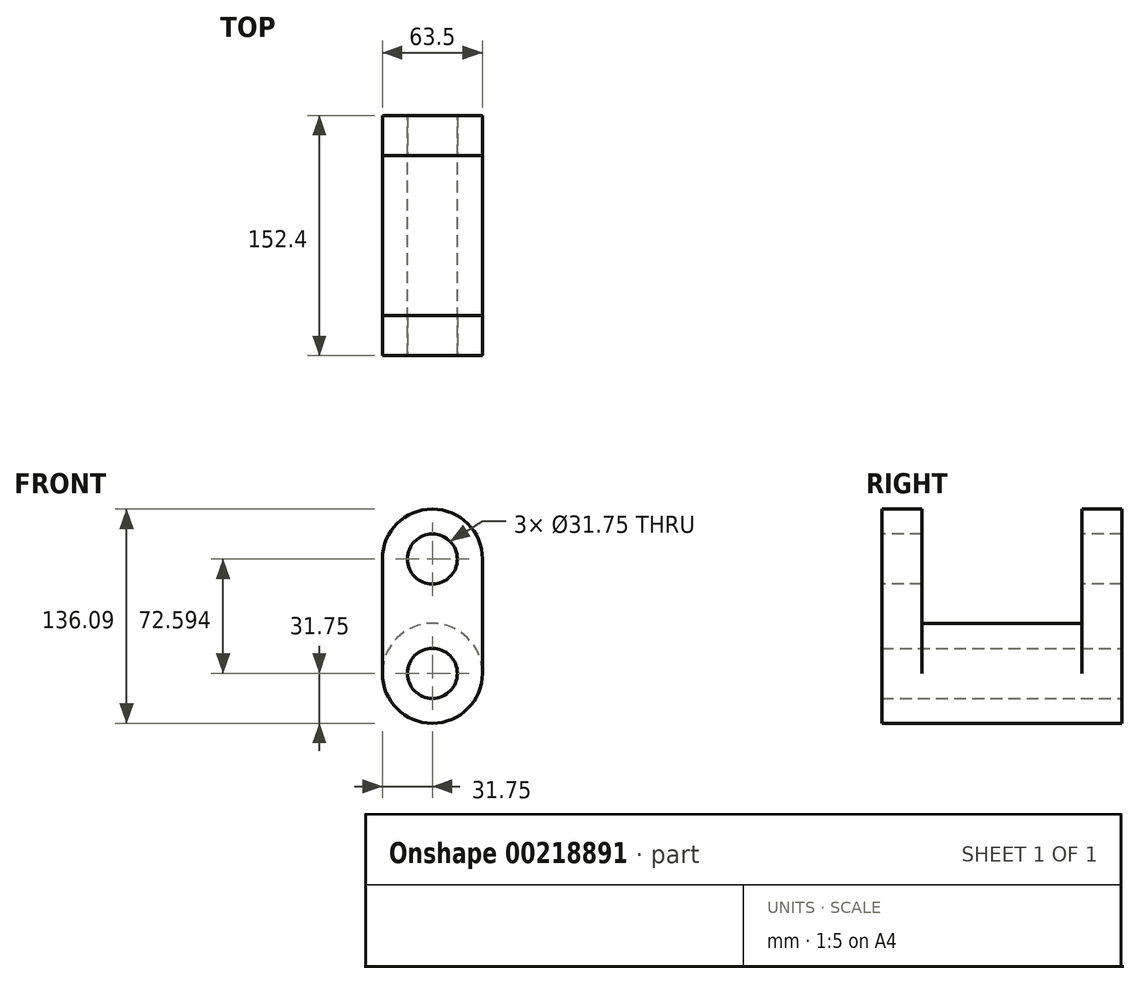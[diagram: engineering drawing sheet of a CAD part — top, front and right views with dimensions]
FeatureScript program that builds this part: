
annotation { "Feature Type Name" : "Feature", "Feature Type Description" : "" }
export const myFeature = defineFeature(function(context is Context, id is Id, definition is map)
    precondition{}
    {
        {
            var Q0;
            Q0=qCreatedBy(makeId("Front.planeOp"),FACE);
            var sketch = newSketch(context, id + "F0", { "sketchPlane" : qUnion([Q0])});
            skCircle(sketch, "E0", {"center": v(0, 0) * mm, "radius": 15.87 * mm});
            skCircle(sketch, "E1", {"center": v(0, 0) * mm, "radius": 31.75 * mm});
            skSolve(sketch);
        }
        {
            var Q0;
            Q0 = qSketchRegion(id + "F0", true);
            extrude(context, id + "F1", {"entities" : qUnion([Q0]), "endBound" : BoundingType.SYMMETRIC, "depth" : 152.4 * mm});
        }
        {
            var Q0;
            Q0=makeQuery(id+"F1.opExtrude","CAP_FACE",FACE,{"disambiguationData":[OSD([sQuery(id+"F0.wireOp",EDGE,"E0"),sQuery(id+"F0.wireOp",EDGE,"E1")])],"isStart":false});
            var sketch = newSketch(context, id + "F2", { "sketchPlane" : qUnion([Q0])});
            skLineSegment(sketch, "E2", {"start": v(-31.75, 0) * mm, "end": v(-31.75, 72.6) * mm});
            skLineSegment(sketch, "E3", {"start": v(-31.75, 72.6) * mm, "end": v(31.75, 72.6) * mm});
            skLineSegment(sketch, "E4", {"start": v(31.75, 72.6) * mm, "end": v(31.75, 0) * mm});
            skCircle(sketch, "E5", {"center": v(0, 72.6) * mm, "radius": 31.75 * mm});
            skSolve(sketch);
        }
        {
            var Q0;
            Q0 = qSketchRegion(id + "F2", true);
            var Q1;
            {var subQ0=sQuery(id+"F2.wireOp",EDGE,"E2");Q1=makeQuery(id+"F2.imprint","IMPRINT",FACE,{"disambiguationData":[TD([[makeQuery(id+"F2.imprint","IMPRINT",EDGE,{"derivedFrom":subQ0}),-1.0]])]});}
            extrude(context, id + "F3", {"entities" : qUnion([Q0, Q1]), "oppositeDirection" : true, "depth" : 25.4 * mm});
        }
        {
            var Q0;
            Q0=makeQuery(id+"F3.opExtrude","SWEPT_BODY",BODY,{"disambiguationData":[OSD([sQuery(id+"F0.wireOp",EDGE,"E1"),sQuery(id+"F2.wireOp",EDGE,"E2"),sQuery(id+"F2.wireOp",EDGE,"E4"),sQuery(id+"F2.wireOp",EDGE,"E5")])]});
            var Q1;
            Q1=qCreatedBy(makeId("Front.planeOp"),FACE);
            mirror(context, id + "F4", {"operationType" : NewBodyOperationType.ADD, "entities" : qUnion([Q0]), "mirrorPlane" : qUnion([Q1])});
        }
        {
            var Q0;
            {var subQ0=sQuery(id+"F0.wireOp",EDGE,"E1");Q0=makeQuery(id+"F4.boolean.opBoolean","MERGE",FACE,{"derivedFrom":[makeQuery(id+"F1.opExtrude","CAP_FACE",FACE,{"disambiguationData":[OSD([sQuery(id+"F0.wireOp",EDGE,"E0"),subQ0])],"isStart":false}),makeQuery(id+"F3.opExtrude","CAP_FACE",FACE,{"disambiguationData":[OSD([subQ0,sQuery(id+"F2.wireOp",EDGE,"E2"),sQuery(id+"F2.wireOp",EDGE,"E4"),sQuery(id+"F2.wireOp",EDGE,"E5")])],"isStart":true})]});}
            var sketch = newSketch(context, id + "F5", { "sketchPlane" : qUnion([Q0])});
            skCircle(sketch, "E6", {"center": v(0, 72.6) * mm, "radius": 15.88 * mm});
            skSolve(sketch);
        }
        {
            var Q0;
            Q0 = qSketchRegion(id + "F5", true);
            extrude(context, id + "F6", {"entities" : qUnion([Q0]), "operationType" : NewBodyOperationType.REMOVE, "endBound" : BoundingType.THROUGH_ALL, "oppositeDirection" : true, "depth" : 25.4 * mm});
        }
    });
